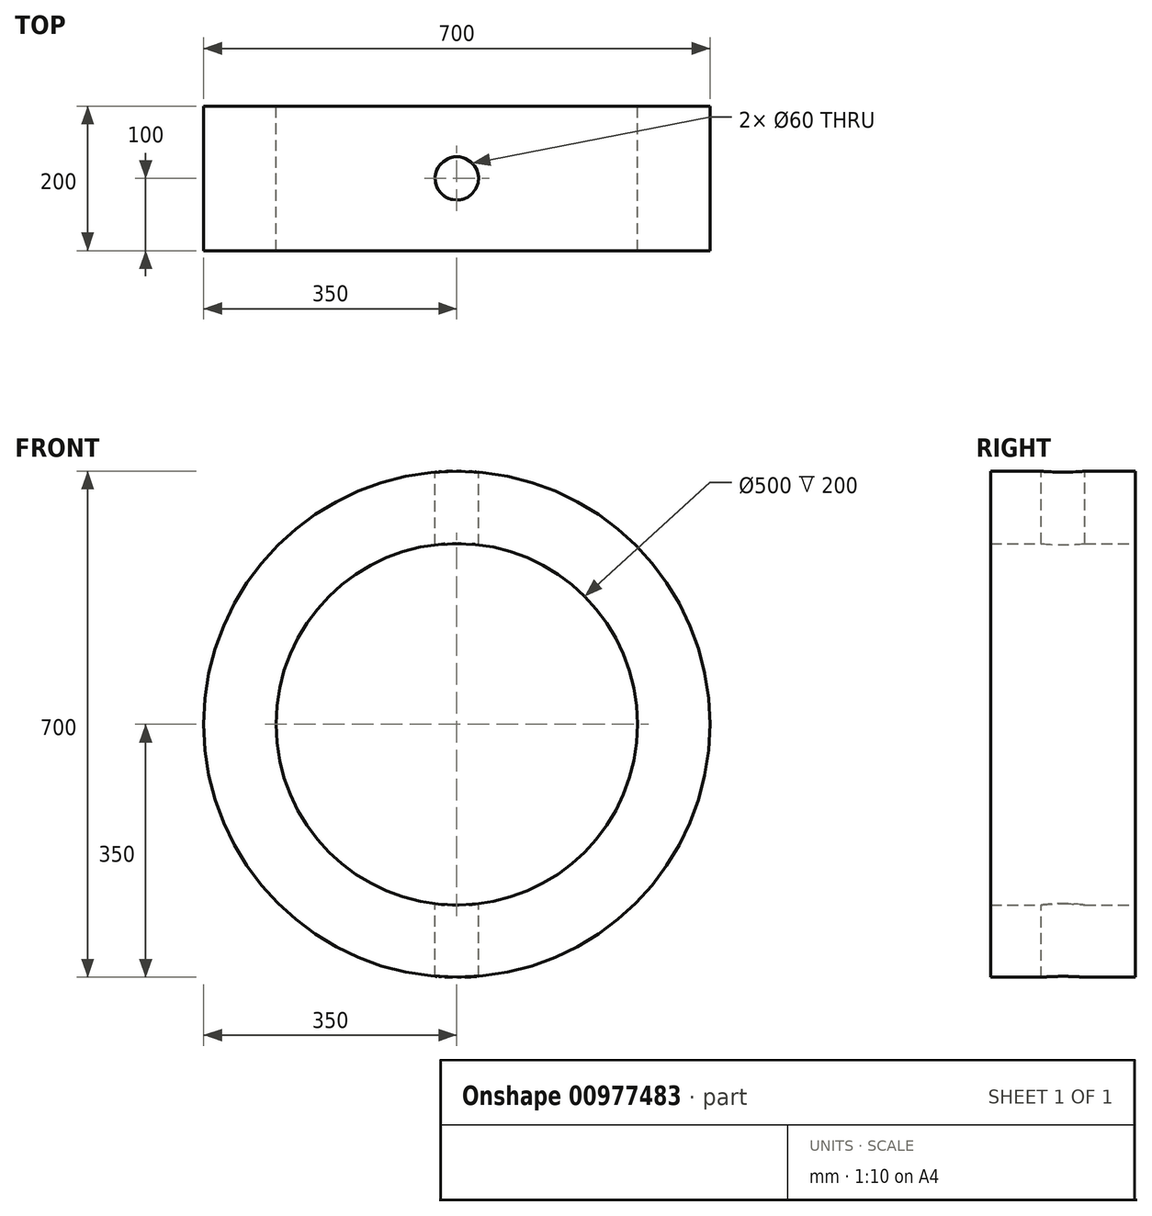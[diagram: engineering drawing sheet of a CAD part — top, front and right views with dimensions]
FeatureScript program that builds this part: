
annotation { "Feature Type Name" : "Feature", "Feature Type Description" : "" }
export const myFeature = defineFeature(function(context is Context, id is Id, definition is map)
    precondition{}
    {
        {
            var Q0;
            Q0=qCreatedBy(makeId("Front.planeOp"),FACE);
            var sketch = newSketch(context, id + "F0", { "sketchPlane" : qUnion([Q0])});
            skCircle(sketch, "E0", {"center": v(0, 0) * mm, "radius": 350 * mm});
            skCircle(sketch, "E1", {"center": v(0, 0) * mm, "radius": 250 * mm});
            skSolve(sketch);
        }
        {
            var Q0;
            Q0 = qSketchRegion(id + "F0", true);
            extrude(context, id + "F1", {"entities" : qUnion([Q0]), "depth" : 200 * mm, "offsetDistance" : 25 * mm});
        }
        {
            var Q0;
            Q0=qCreatedBy(makeId("Top.planeOp"),FACE);
            var sketch = newSketch(context, id + "F2", { "sketchPlane" : qUnion([Q0])});
            skCircle(sketch, "E2", {"center": v(0, -100) * mm, "radius": 30 * mm});
            skSolve(sketch);
        }
        {
            var Q0;
            Q0 = qSketchRegion(id + "F2", true);
            extrude(context, id + "F3", {"entities" : qUnion([Q0]), "operationType" : NewBodyOperationType.REMOVE, "endBound" : BoundingType.SYMMETRIC, "oppositeDirection" : true, "depth" : 1000 * mm, "offsetDistance" : 25 * mm});
        }
    });
